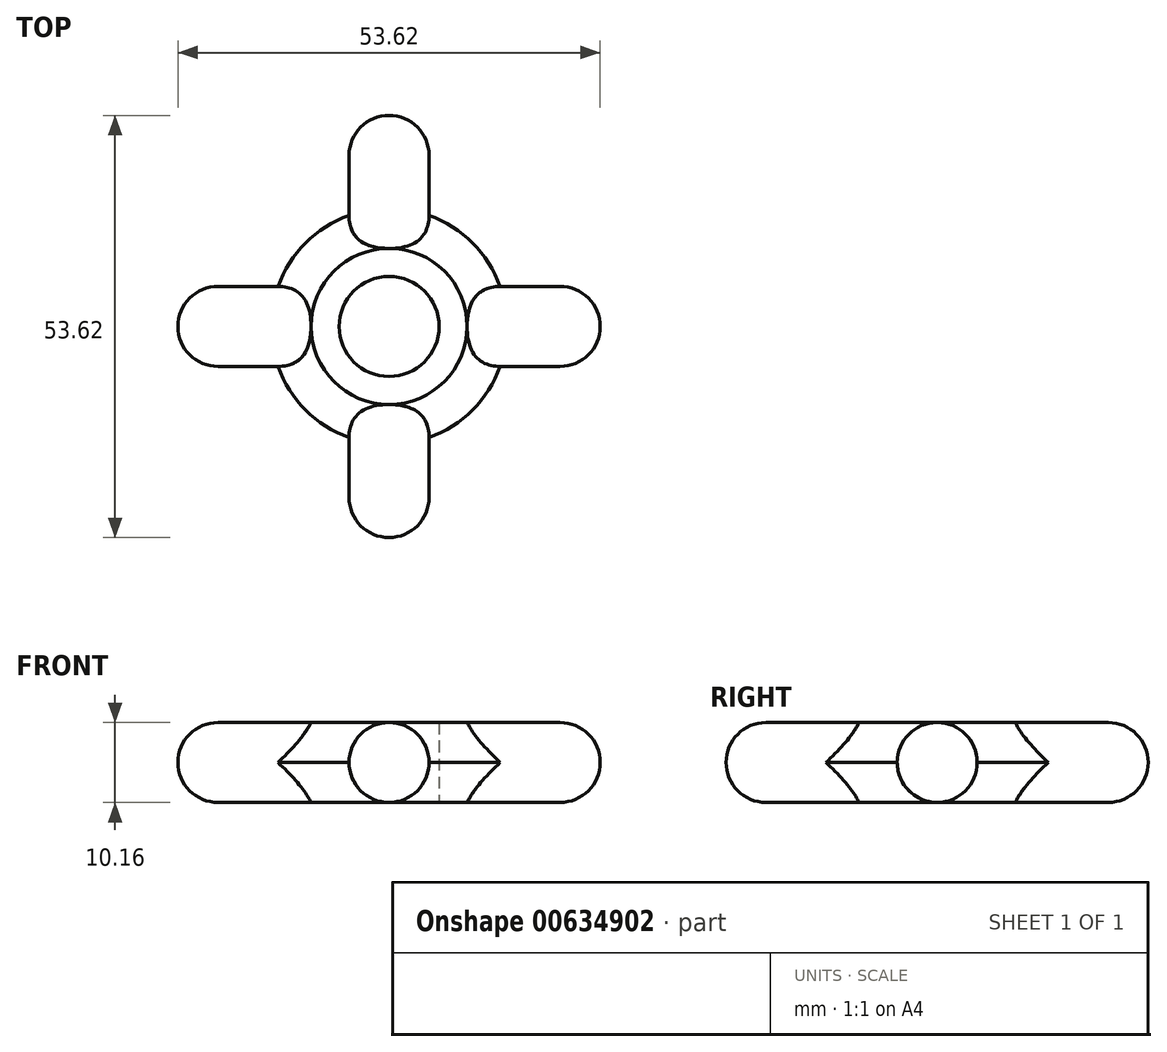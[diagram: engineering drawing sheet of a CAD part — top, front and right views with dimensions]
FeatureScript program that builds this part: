
annotation { "Feature Type Name" : "Feature", "Feature Type Description" : "" }
export const myFeature = defineFeature(function(context is Context, id is Id, definition is map)
    precondition{}
    {
        {
            var Q0;
            Q0=qCreatedBy(makeId("Top.planeOp"),FACE);
            var sketch = newSketch(context, id + "F0", { "sketchPlane" : qUnion([Q0])});
            skCircle(sketch, "E0", {"center": v(0, 0) * mm, "radius": 6.35 * mm});
            skCircle(sketch, "E1", {"center": v(0, 0) * mm, "radius": 3.17 * mm});
            skSolve(sketch);
        }
        {
            var Q0;
            Q0=qCreatedBy(makeId("Top.planeOp"),FACE);
            var sketch = newSketch(context, id + "F1", { "sketchPlane" : qUnion([Q0])});
            skCircle(sketch, "E2", {"center": v(0, 0) * mm, "radius": 15 * mm});
            skLineSegment(sketch, "E3", {"start": v(5.08, 14.11) * mm, "end": v(5.08, 21.73) * mm});
            skLineSegment(sketch, "E4", {"start": v(0, 26.81) * mm, "end": v(0, 26.81) * mm});
            skLineSegment(sketch, "E5", {"start": v(-5.08, 21.73) * mm, "end": v(-5.08, 14.11) * mm});
            skPoint(sketch, "E6.visualSharp", {"position": v(5.08, 26.81) * mm});
            skArc(sketch, "E6.filletArc", {"start": v(5.08, 21.73) * mm, "mid": v(3.6, 25.33) * mm, "end": v(0, 26.81) * mm});
            skPoint(sketch, "E7.visualSharp", {"position": v(-5.08, 26.81) * mm});
            skArc(sketch, "E7.filletArc", {"start": v(0, 26.81) * mm, "mid": v(-3.6, 25.33) * mm, "end": v(-5.08, 21.73) * mm});
            skLineSegment(sketch, "E8", {"start": v(14.11, 5.08) * mm, "end": v(21.73, 5.08) * mm});
            skLineSegment(sketch, "E9", {"start": v(26.81, 0) * mm, "end": v(26.81, 0) * mm});
            skLineSegment(sketch, "E10", {"start": v(21.73, -5.08) * mm, "end": v(14.11, -5.08) * mm});
            skPoint(sketch, "E11.visualSharp", {"position": v(26.81, -5.08) * mm});
            skArc(sketch, "E11.filletArc", {"start": v(21.73, -5.08) * mm, "mid": v(25.33, -3.6) * mm, "end": v(26.81, 0) * mm});
            skPoint(sketch, "E12.visualSharp", {"position": v(26.81, 5.08) * mm});
            skArc(sketch, "E12.filletArc", {"start": v(26.81, 0) * mm, "mid": v(25.33, 3.6) * mm, "end": v(21.73, 5.08) * mm});
            skLineSegment(sketch, "E13", {"start": v(-5.08, -14.11) * mm, "end": v(-5.08, -21.73) * mm});
            skLineSegment(sketch, "E14", {"start": v(0, -26.81) * mm, "end": v(0, -26.81) * mm});
            skLineSegment(sketch, "E15", {"start": v(5.08, -21.73) * mm, "end": v(5.08, -14.11) * mm});
            skPoint(sketch, "E16.visualSharp", {"position": v(5.08, -26.81) * mm});
            skArc(sketch, "E16.filletArc", {"start": v(0, -26.81) * mm, "mid": v(3.6, -25.33) * mm, "end": v(5.08, -21.73) * mm});
            skPoint(sketch, "E17.visualSharp", {"position": v(-5.08, -26.81) * mm});
            skArc(sketch, "E17.filletArc", {"start": v(-5.08, -21.73) * mm, "mid": v(-3.6, -25.33) * mm, "end": v(0, -26.81) * mm});
            skLineSegment(sketch, "E18", {"start": v(-14.11, -5.08) * mm, "end": v(-21.73, -5.08) * mm});
            skLineSegment(sketch, "E19", {"start": v(-26.81, 0) * mm, "end": v(-26.81, 0) * mm});
            skLineSegment(sketch, "E20", {"start": v(-21.73, 5.08) * mm, "end": v(-14.11, 5.08) * mm});
            skPoint(sketch, "E21.visualSharp", {"position": v(-26.81, 5.08) * mm});
            skArc(sketch, "E21.filletArc", {"start": v(-21.73, 5.08) * mm, "mid": v(-25.33, 3.6) * mm, "end": v(-26.81, 0) * mm});
            skPoint(sketch, "E22.visualSharp", {"position": v(-26.81, -5.08) * mm});
            skArc(sketch, "E22.filletArc", {"start": v(-26.81, 0) * mm, "mid": v(-25.33, -3.6) * mm, "end": v(-21.73, -5.08) * mm});
            skSolve(sketch);
        }
        {
            var Q0;
            Q0=makeQuery(id+"F0.imprint","IMPRINT",FACE,{"disambiguationData":[TD([[makeQuery(id+"F0.imprint","IMPRINT",EDGE,{"derivedFrom":sQuery(id+"F0.wireOp",EDGE,"E0")}),1.0]])]});
            var Q1;
            Q1=makeQuery(id+"F0.imprint","IMPRINT",FACE,{"disambiguationData":[TD([[makeQuery(id+"F0.imprint","IMPRINT",EDGE,{"derivedFrom":sQuery(id+"F0.wireOp",EDGE,"E1")}),1.0]])]});
            var Q2;
            {var subQ1=sQuery(id+"F1.wireOp",EDGE,"E3");Q2=makeQuery(id+"F1.imprint","IMPRINT",FACE,{"disambiguationData":[TD([[makeQuery(id+"F1.imprint","IMPRINT",EDGE,{"derivedFrom":subQ1}),1.0]])]});}
            var Q3;
            {var subQ1=sQuery(id+"F1.wireOp",EDGE,"E18");Q3=makeQuery(id+"F1.imprint","IMPRINT",FACE,{"disambiguationData":[TD([[makeQuery(id+"F1.imprint","IMPRINT",EDGE,{"derivedFrom":subQ1}),-1.0]])]});}
            var Q4;
            {var subQ1=sQuery(id+"F1.wireOp",EDGE,"E13");Q4=makeQuery(id+"F1.imprint","IMPRINT",FACE,{"disambiguationData":[TD([[makeQuery(id+"F1.imprint","IMPRINT",EDGE,{"derivedFrom":subQ1}),1.0]])]});}
            var Q5;
            {var subQ1=sQuery(id+"F1.wireOp",EDGE,"E8");Q5=makeQuery(id+"F1.imprint","IMPRINT",FACE,{"disambiguationData":[TD([[makeQuery(id+"F1.imprint","IMPRINT",EDGE,{"derivedFrom":subQ1}),-1.0]])]});}
            var Q6;
            {var subQ0=sQuery(id+"F1.wireOp",EDGE,"E2");var subQ4=makeQuery(id+"F1.imprint","INTERSECT",VERTEX,{"derivedFrom":[subQ0,sQuery(id+"F1.wireOp",EDGE,"E3")]});Q6=makeQuery(id+"F1.imprint","IMPRINT",FACE,{"disambiguationData":[TD([[makeQuery(id+"F1.imprint","IMPRINT",EDGE,{"disambiguationData":[TD([[subQ4,1.0]])],"derivedFrom":subQ0}),1.0]])]});}
            extrude(context, id + "F2", {"entities" : qUnion([Q0, Q1, Q2, Q3, Q4, Q5, Q6]), "depth" : 10.16 * mm, "offsetDistance" : 25.4 * mm});
        }
        {
            var Q0;
            {var subQ0=sQuery(id+"F1.wireOp",EDGE,"E2");Q0=makeQuery(id+"F2.opExtrude","CAP_EDGE",EDGE,{"disambiguationData":[OSD([subQ0]),TDD([makeQuery(id+"F1.imprint","IMPRINT",EDGE,{"disambiguationData":[TD([[makeQuery(id+"F1.imprint","INTERSECT",VERTEX,{"derivedFrom":[subQ0,sQuery(id+"F1.wireOp",EDGE,"E5")]}),-1.0]])],"derivedFrom":subQ0})])],"isStart":false});}
            var Q1;
            {var subQ0=sQuery(id+"F1.wireOp",EDGE,"E2");Q1=makeQuery(id+"F2.opExtrude","CAP_EDGE",EDGE,{"disambiguationData":[OSD([subQ0]),TDD([makeQuery(id+"F1.imprint","IMPRINT",EDGE,{"disambiguationData":[TD([[makeQuery(id+"F1.imprint","INTERSECT",VERTEX,{"derivedFrom":[subQ0,sQuery(id+"F1.wireOp",EDGE,"E5")]}),-1.0]])],"derivedFrom":subQ0})])],"isStart":true});}
            var Q2;
            {var subQ0=sQuery(id+"F1.wireOp",EDGE,"E2");Q2=makeQuery(id+"F2.opExtrude","CAP_EDGE",EDGE,{"disambiguationData":[OSD([subQ0]),TDD([makeQuery(id+"F1.imprint","IMPRINT",EDGE,{"disambiguationData":[TD([[makeQuery(id+"F1.imprint","INTERSECT",VERTEX,{"derivedFrom":[subQ0,sQuery(id+"F1.wireOp",EDGE,"E13")]}),1.0]])],"derivedFrom":subQ0})])],"isStart":true});}
            var Q3;
            {var subQ0=sQuery(id+"F1.wireOp",EDGE,"E2");Q3=makeQuery(id+"F2.opExtrude","CAP_EDGE",EDGE,{"disambiguationData":[OSD([subQ0]),TDD([makeQuery(id+"F1.imprint","IMPRINT",EDGE,{"disambiguationData":[TD([[makeQuery(id+"F1.imprint","INTERSECT",VERTEX,{"derivedFrom":[subQ0,sQuery(id+"F1.wireOp",EDGE,"E13")]}),1.0]])],"derivedFrom":subQ0})])],"isStart":false});}
            var Q4;
            {var subQ0=sQuery(id+"F1.wireOp",EDGE,"E2");Q4=makeQuery(id+"F2.opExtrude","CAP_EDGE",EDGE,{"disambiguationData":[OSD([subQ0]),TDD([makeQuery(id+"F1.imprint","IMPRINT",EDGE,{"disambiguationData":[TD([[makeQuery(id+"F1.imprint","INTERSECT",VERTEX,{"derivedFrom":[subQ0,sQuery(id+"F1.wireOp",EDGE,"E10")]}),1.0]])],"derivedFrom":subQ0})])],"isStart":true});}
            var Q5;
            {var subQ0=sQuery(id+"F1.wireOp",EDGE,"E2");Q5=makeQuery(id+"F2.opExtrude","CAP_EDGE",EDGE,{"disambiguationData":[OSD([subQ0]),TDD([makeQuery(id+"F1.imprint","IMPRINT",EDGE,{"disambiguationData":[TD([[makeQuery(id+"F1.imprint","INTERSECT",VERTEX,{"derivedFrom":[subQ0,sQuery(id+"F1.wireOp",EDGE,"E10")]}),1.0]])],"derivedFrom":subQ0})])],"isStart":false});}
            var Q6;
            {var subQ0=sQuery(id+"F1.wireOp",EDGE,"E2");Q6=makeQuery(id+"F2.opExtrude","CAP_EDGE",EDGE,{"disambiguationData":[OSD([subQ0]),TDD([makeQuery(id+"F1.imprint","IMPRINT",EDGE,{"disambiguationData":[TD([[makeQuery(id+"F1.imprint","INTERSECT",VERTEX,{"derivedFrom":[subQ0,sQuery(id+"F1.wireOp",EDGE,"E3")]}),1.0]])],"derivedFrom":subQ0})])],"isStart":true});}
            var Q7;
            {var subQ0=sQuery(id+"F1.wireOp",EDGE,"E2");Q7=makeQuery(id+"F2.opExtrude","CAP_EDGE",EDGE,{"disambiguationData":[OSD([subQ0]),TDD([makeQuery(id+"F1.imprint","IMPRINT",EDGE,{"disambiguationData":[TD([[makeQuery(id+"F1.imprint","INTERSECT",VERTEX,{"derivedFrom":[subQ0,sQuery(id+"F1.wireOp",EDGE,"E3")]}),1.0]])],"derivedFrom":subQ0})])],"isStart":false});}
            chamfer(context, id + "F3", {"entities" : qUnion([Q0, Q1, Q2, Q3, Q4, Q5, Q6, Q7]), "width" : 5.08 * mm, "tangentPropagation" : true});
        }
        {
            var Q0;
            Q0=makeQuery(id+"F2.opExtrude","CAP_EDGE",EDGE,{"disambiguationData":[OSD([sQuery(id+"F1.wireOp",EDGE,"E5")])],"isStart":false});
            var Q1;
            Q1=makeQuery(id+"F2.opExtrude","CAP_EDGE",EDGE,{"disambiguationData":[OSD([sQuery(id+"F1.wireOp",EDGE,"E5")])],"isStart":true});
            var Q2;
            Q2=makeQuery(id+"F2.opExtrude","CAP_EDGE",EDGE,{"disambiguationData":[OSD([sQuery(id+"F1.wireOp",EDGE,"E18")])],"isStart":false});
            var Q3;
            Q3=makeQuery(id+"F2.opExtrude","CAP_EDGE",EDGE,{"disambiguationData":[OSD([sQuery(id+"F1.wireOp",EDGE,"E18")])],"isStart":true});
            var Q4;
            Q4=makeQuery(id+"F2.opExtrude","CAP_EDGE",EDGE,{"disambiguationData":[OSD([sQuery(id+"F1.wireOp",EDGE,"E8")])],"isStart":false});
            var Q5;
            Q5=makeQuery(id+"F2.opExtrude","CAP_EDGE",EDGE,{"disambiguationData":[OSD([sQuery(id+"F1.wireOp",EDGE,"E8")])],"isStart":true});
            var Q6;
            Q6=makeQuery(id+"F2.opExtrude","CAP_EDGE",EDGE,{"disambiguationData":[OSD([sQuery(id+"F1.wireOp",EDGE,"E13")])],"isStart":false});
            var Q7;
            Q7=makeQuery(id+"F2.opExtrude","CAP_EDGE",EDGE,{"disambiguationData":[OSD([sQuery(id+"F1.wireOp",EDGE,"E13")])],"isStart":true});
            fillet(context, id + "F4", {"entities" : qUnion([Q0, Q1, Q2, Q3, Q4, Q5, Q6, Q7]), "radius" : 5.08 * mm, "tangentPropagation" : true, "allowEdgeOverflow" : false});
        }
    });
